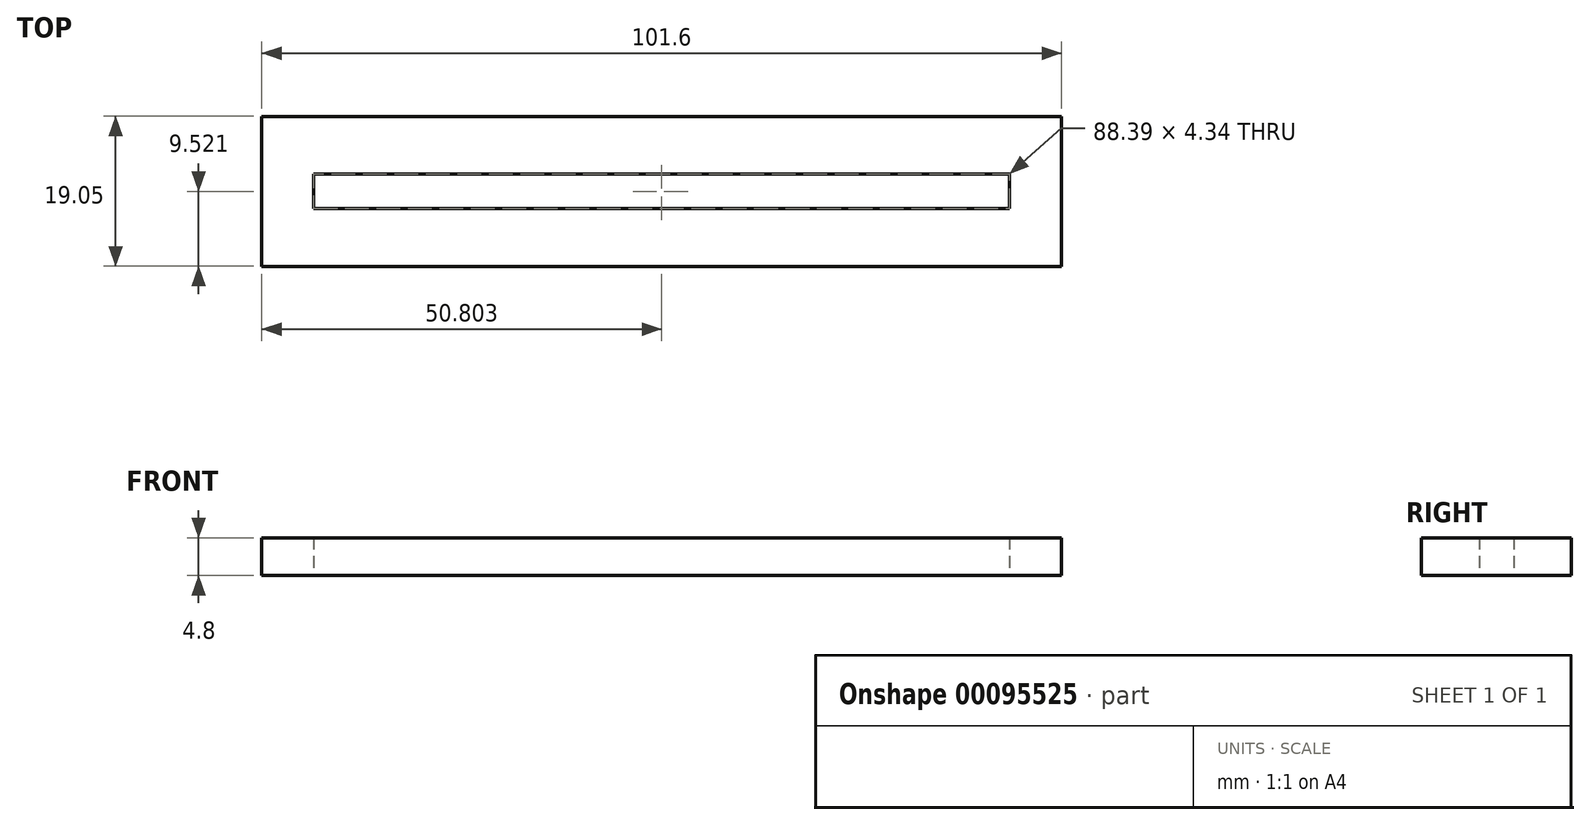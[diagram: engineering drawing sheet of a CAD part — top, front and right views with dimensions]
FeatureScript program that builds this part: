
annotation { "Feature Type Name" : "Feature", "Feature Type Description" : "" }
export const myFeature = defineFeature(function(context is Context, id is Id, definition is map)
    precondition{}
    {
        {
            var Q0;
            Q0=qCreatedBy(makeId("Top.planeOp"),FACE);
            var sketch = newSketch(context, id + "F0", { "sketchPlane" : qUnion([Q0])});
            skLineSegment(sketch, "E0.bottom", {"start": v(-39.26, 32.74) * mm, "end": v(62.34, 32.74) * mm});
            skLineSegment(sketch, "E0.top", {"start": v(-39.26, 13.69) * mm, "end": v(62.34, 13.69) * mm});
            skLineSegment(sketch, "E0.left", {"start": v(-39.26, 32.74) * mm, "end": v(-39.26, 13.69) * mm});
            skLineSegment(sketch, "E0.right", {"start": v(62.34, 32.74) * mm, "end": v(62.34, 13.69) * mm});
            skLineSegment(sketch, "E1.0", {"start": v(-32.65, 32.74) * mm, "end": v(-32.65, 13.69) * mm, "construction": true});
            skLineSegment(sketch, "E2.0", {"start": v(55.74, 32.74) * mm, "end": v(55.74, 13.69) * mm, "construction": true});
            skLineSegment(sketch, "E3", {"start": v(-32.65, 23.21) * mm, "end": v(55.74, 23.21) * mm, "construction": true});
            skLineSegment(sketch, "E4", {"start": v(55.74, 23.21) * mm, "end": v(55.74, 25.38) * mm});
            skLineSegment(sketch, "E5.MirrorCS", {"start": v(55.74, 23.21) * mm, "end": v(55.74, 21.04) * mm});
            skLineSegment(sketch, "E6", {"start": v(55.74, 25.38) * mm, "end": v(-32.65, 25.38) * mm});
            skLineSegment(sketch, "E7", {"start": v(-32.65, 25.38) * mm, "end": v(-32.65, 23.21) * mm});
            skLineSegment(sketch, "E8", {"start": v(55.74, 21.04) * mm, "end": v(-32.65, 21.04) * mm});
            skLineSegment(sketch, "E9", {"start": v(-32.65, 21.04) * mm, "end": v(-32.65, 23.21) * mm});
            skSolve(sketch);
        }
        {
            var Q0;
            Q0=makeQuery(id+"F0.imprint","IMPRINT",FACE,{"disambiguationData":[TD([[makeQuery(id+"F0.imprint","IMPRINT",EDGE,{"derivedFrom":sQuery(id+"F0.wireOp",EDGE,"E0.bottom")}),-1.0]])]});
            extrude(context, id + "F1", {"entities" : qUnion([Q0]), "depth" : 4.8 * mm});
        }
    });
